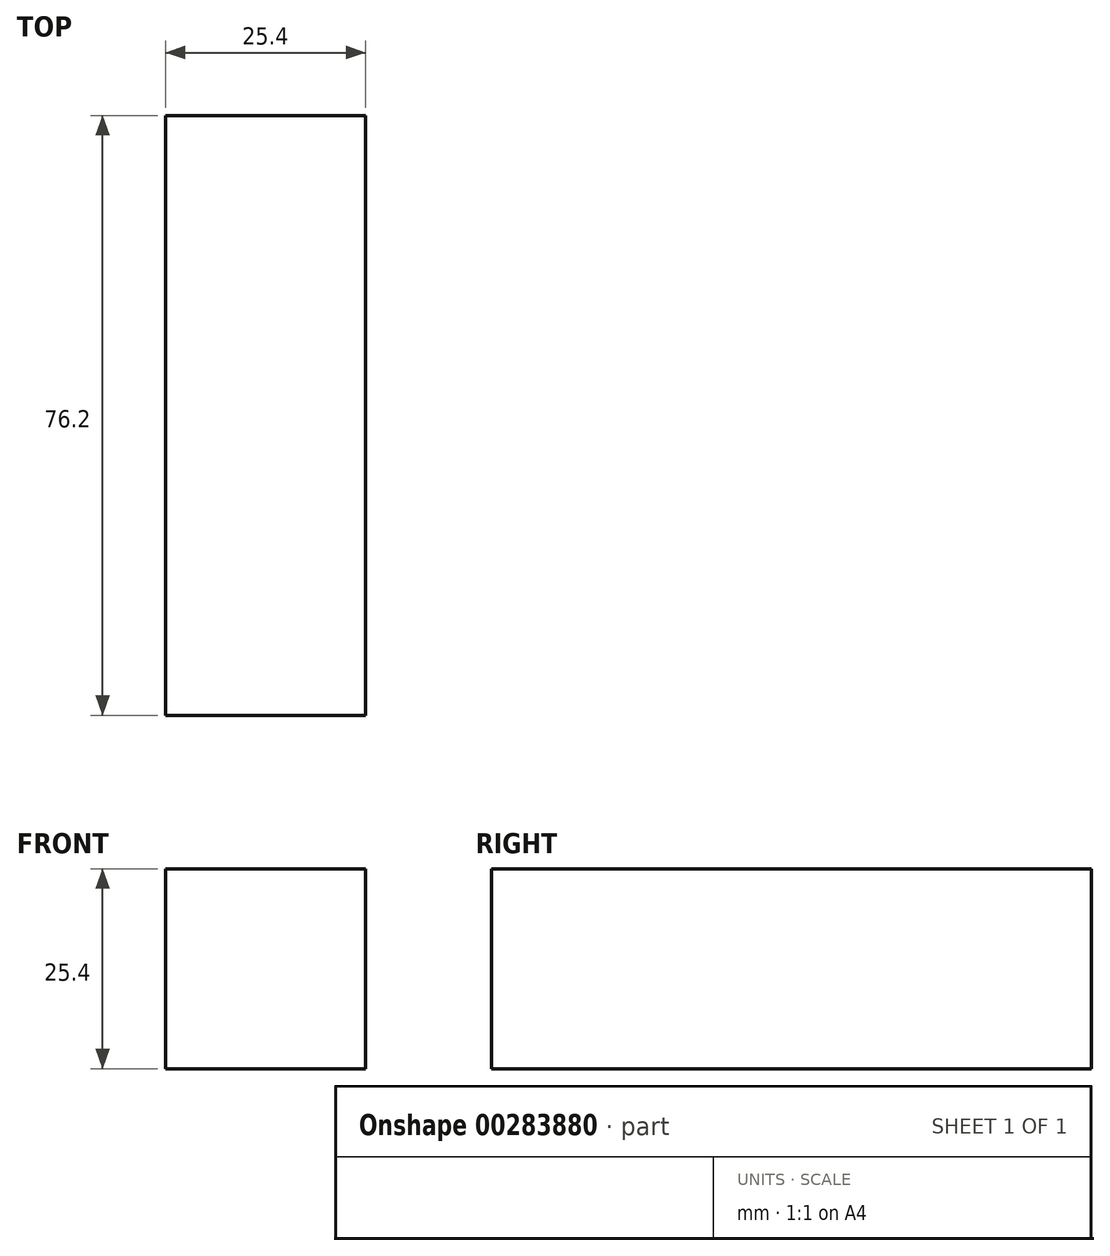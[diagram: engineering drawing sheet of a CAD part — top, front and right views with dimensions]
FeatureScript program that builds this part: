
annotation { "Feature Type Name" : "Feature", "Feature Type Description" : "" }
export const myFeature = defineFeature(function(context is Context, id is Id, definition is map)
    precondition{}
    {
        {
            var Q0;
            Q0=qCreatedBy(makeId("Front.planeOp"),FACE);
            var sketch = newSketch(context, id + "F0", { "sketchPlane" : qUnion([Q0])});
            skLineSegment(sketch, "E0", {"start": v(0, 0) * mm, "end": v(0, 25.4) * mm});
            skLineSegment(sketch, "E1", {"start": v(0, 25.4) * mm, "end": v(-25.4, 25.4) * mm});
            skLineSegment(sketch, "E2", {"start": v(-25.4, 25.4) * mm, "end": v(-25.4, 0) * mm});
            skLineSegment(sketch, "E3", {"start": v(-25.4, 0) * mm, "end": v(0, 0) * mm});
            skSolve(sketch);
        }
        {
            var Q0;
            Q0 = qSketchRegion(id + "F0", true);
            extrude(context, id + "F1", {"entities" : qUnion([Q0]), "depth" : 76.2 * mm});
        }
    });
